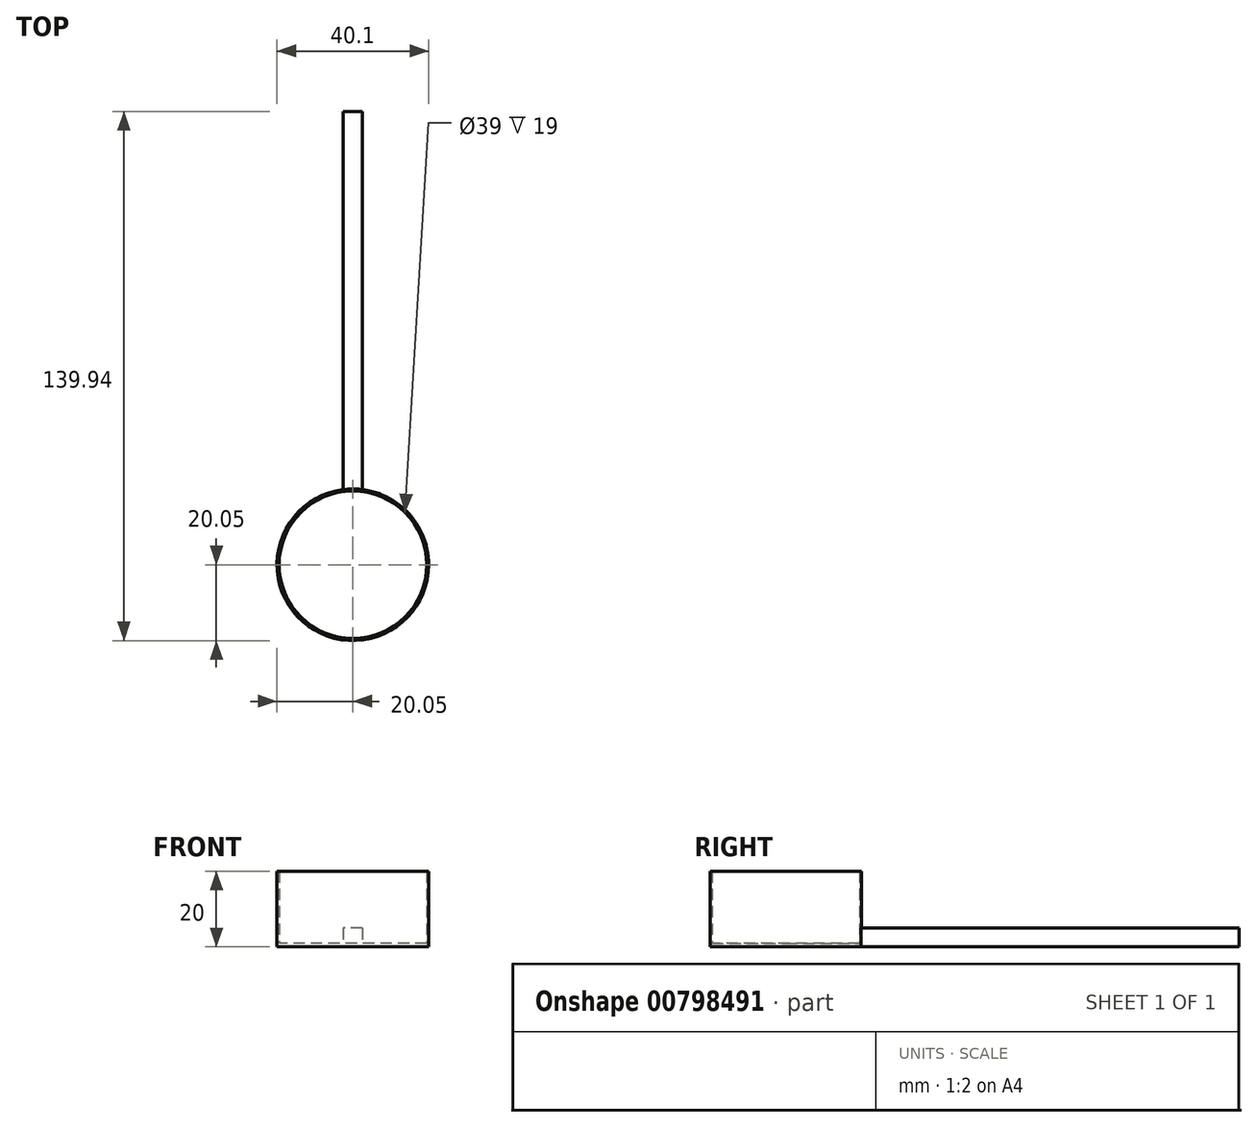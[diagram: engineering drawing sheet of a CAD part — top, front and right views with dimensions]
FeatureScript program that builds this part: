
annotation { "Feature Type Name" : "Feature", "Feature Type Description" : "" }
export const myFeature = defineFeature(function(context is Context, id is Id, definition is map)
    precondition{}
    {
        {
            var Q0;
            Q0=qCreatedBy(makeId("Top.planeOp"),FACE);
            var sketch = newSketch(context, id + "F0", { "sketchPlane" : qUnion([Q0])});
            skCircle(sketch, "E0", {"center": v(0, 0) * mm, "radius": 20.05 * mm});
            skLineSegment(sketch, "E1.top", {"start": v(2.5, 119.9) * mm, "end": v(-2.5, 119.9) * mm});
            skLineSegment(sketch, "E1.left", {"start": v(2.5, 19.9) * mm, "end": v(2.5, 119.9) * mm});
            skLineSegment(sketch, "E1.right", {"start": v(-2.5, 19.9) * mm, "end": v(-2.5, 119.9) * mm});
            skSolve(sketch);
        }
        {
            var Q0;
            {var subQ0=sQuery(id+"F0.wireOp",EDGE,"E0");var subQ1=makeQuery(id+"F0.imprint","INTERSECT",VERTEX,{"derivedFrom":[subQ0,sQuery(id+"F0.wireOp",EDGE,"E1.left")]});Q0=makeQuery(id+"F0.imprint","IMPRINT",FACE,{"disambiguationData":[TD([[makeQuery(id+"F0.imprint","IMPRINT",EDGE,{"disambiguationData":[TD([[subQ1,-1.0]])],"derivedFrom":subQ0}),1.0]])]});}
            extrude(context, id + "F1", {"entities" : qUnion([Q0]), "depth" : 1 * mm, "offsetDistance" : 25 * mm});
        }
        {
            var Q0;
            Q0=makeQuery(id+"F0.imprint","IMPRINT",FACE,{"disambiguationData":[TD([[makeQuery(id+"F0.imprint","IMPRINT",EDGE,{"derivedFrom":sQuery(id+"F0.wireOp",EDGE,"E1.top")}),1.0]])]});
            extrude(context, id + "F2", {"entities" : qUnion([Q0]), "operationType" : NewBodyOperationType.ADD, "depth" : 5 * mm, "offsetDistance" : 25 * mm});
        }
        {
            var Q0;
            Q0=makeQuery(id+"F1.opExtrude","CAP_FACE",FACE,{"disambiguationData":[OSD([sQuery(id+"F0.wireOp",EDGE,"E0")])],"isStart":false});
            var sketch = newSketch(context, id + "F3", { "sketchPlane" : qUnion([Q0])});
            skCircle(sketch, "E2", {"center": v(0, 0) * mm, "radius": 19.5 * mm});
            skCircle(sketch, "E3", {"center": v(0, 0) * mm, "radius": 20.05 * mm});
            skSolve(sketch);
        }
        {
            var Q0;
            Q0 = qSketchRegion(id + "F3", true);
            extrude(context, id + "F4", {"entities" : qUnion([Q0]), "operationType" : NewBodyOperationType.ADD, "depth" : 19 * mm, "offsetDistance" : 25 * mm});
        }
    });
